# Revit family: Thorn AXYL GLOW
name_source: partatom
category: Lighting Fixtures
units: mm (PartAtom-declared; Revit-internal decimal feet)

## family parameters
Cut with Voids When Loaded = Yes
Host = Face
Light Source = No
Maintain Annotation Orientation = No
Part Type = Normal
Room Calculation Point = Yes
Round Connector Dimension = Use Diameter
Shared = No

## types (1)
- Thorn AXYL GLOW
    Apparent Load = 10 VA
    Assembly Code = Pr_70_70_48_93
    Body Size = Thorn-Axyl-Glow-Body : Small
    Body Size Large = Thorn-Axyl-Glow-Body : Large
    Body Size Medium = Thorn-Axyl-Glow-Body : Medium
    Body Size Small = Thorn-Axyl-Glow-Body : Small
    Default Elevation = 1000 mm  [stored 3.28084 ft]
    Description = Wall Mounted Decorative Luminaire
    Down = Yes
    Export Type to IFC As = IfcLightFixtureType
    Housing Large = No
    Housing Medium = No
    Housing Small = Yes
    Lamp = LED
    Luminaire Height = 72 mm  [stored 0.23622 ft]
    Luminaire Length = 200 mm  [stored 0.656168 ft]
    Luminaire Width = 60 mm  [stored 0.19685 ft]
    Manufacturer = Thorn Lighting
    Material Housing = Thorn-Aluminium-RAL 7016-Anthracite Grey
    Model = 96700165
    Power Factor = 0.54
    Type IFC Predefined Type = DIRECTIONSOURCE
    Type Image = TLG_AXYL_F_GLOW_S_ANT.jpg
    Type Light Source DOWN = Thorn-Light Source-Axyl-Glow : AXYL GLOW S U/D 2L930 WB HF ANT_photometric_data_DOWN
    Type Light Source UP = Thorn-Light Source-Axyl-Glow : AXYL GLOW S U/D 2L930 WB HF ANT_photometric_data_UP
    URL = https://www.thornlighting.com
    Up and Down = Yes
    Wattage = 5 W

note: [stored X ft] marks values corroborated as IEEE doubles in the binary element streams (Revit-internal decimal feet)

## geometry (parser evidence)
native form markers: Sweep x7
no freeform markers — native parametric forms only
